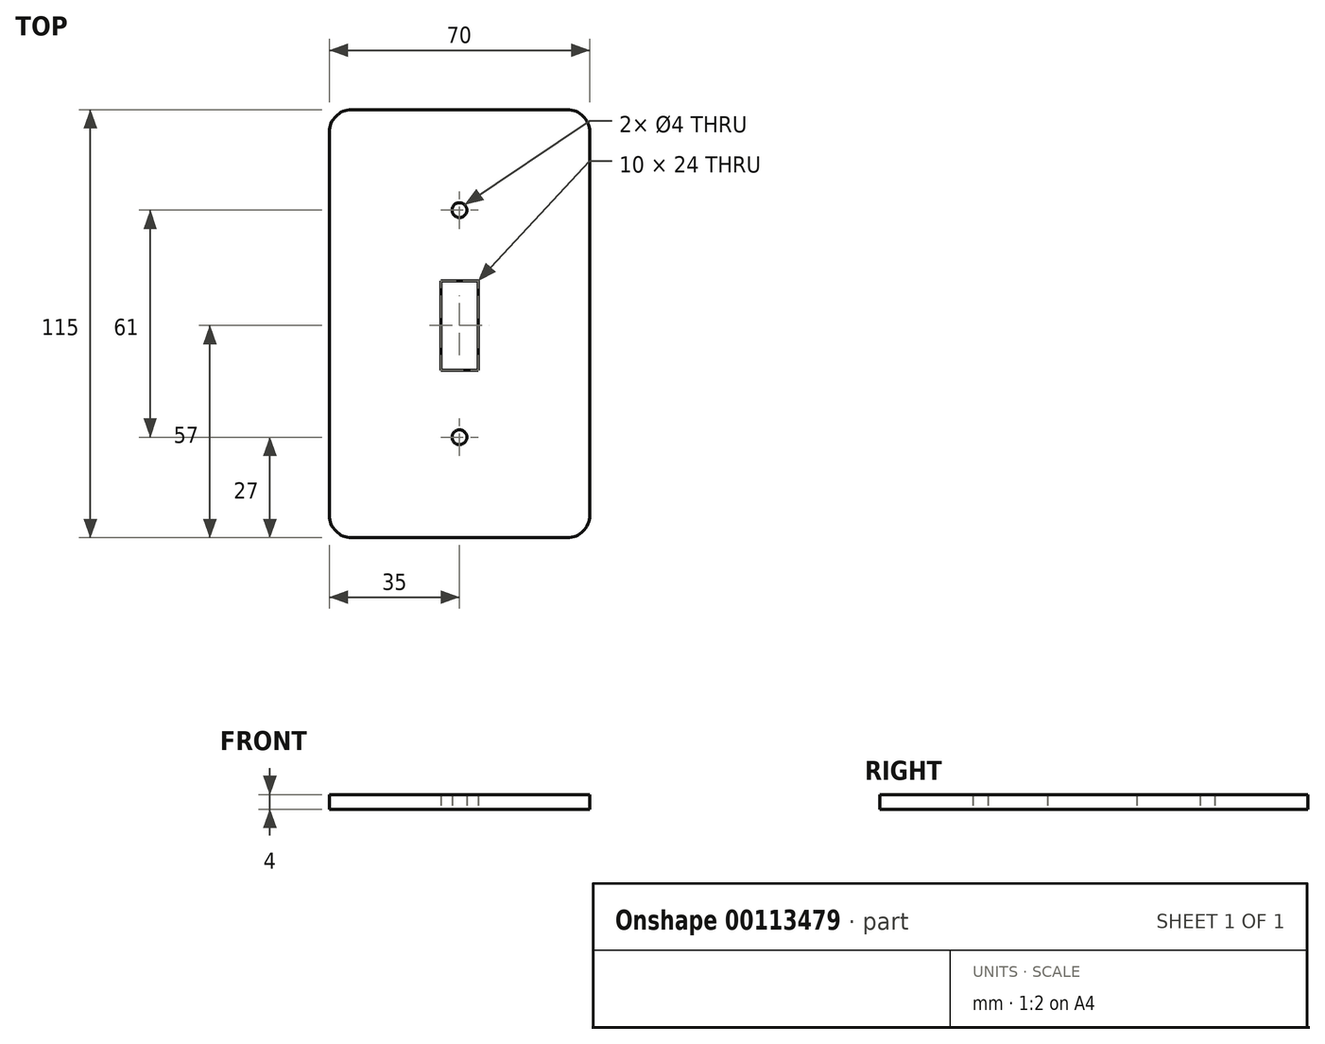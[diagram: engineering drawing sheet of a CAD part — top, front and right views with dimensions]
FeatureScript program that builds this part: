
annotation { "Feature Type Name" : "Feature", "Feature Type Description" : "" }
export const myFeature = defineFeature(function(context is Context, id is Id, definition is map)
    precondition{}
    {
        {
            var Q0;
            Q0=qCreatedBy(makeId("Top.planeOp"),FACE);
            var sketch = newSketch(context, id + "F0", { "sketchPlane" : qUnion([Q0])});
            skLineSegment(sketch, "E0.bottom", {"start": v(0, 0) * mm, "end": v(70, 0) * mm});
            skLineSegment(sketch, "E0.top", {"start": v(0, 115) * mm, "end": v(70, 115) * mm});
            skLineSegment(sketch, "E0.left", {"start": v(0, 0) * mm, "end": v(0, 115) * mm});
            skLineSegment(sketch, "E0.right", {"start": v(70, 0) * mm, "end": v(70, 115) * mm});
            skLineSegment(sketch, "E1.bottom", {"start": v(30, 69) * mm, "end": v(40, 69) * mm});
            skLineSegment(sketch, "E1.top", {"start": v(30, 45) * mm, "end": v(40, 45) * mm});
            skLineSegment(sketch, "E1.left", {"start": v(30, 69) * mm, "end": v(30, 45) * mm});
            skLineSegment(sketch, "E1.right", {"start": v(40, 69) * mm, "end": v(40, 45) * mm});
            skCircle(sketch, "E2", {"center": v(35, 88) * mm, "radius": 2 * mm});
            skCircle(sketch, "E3", {"center": v(35, 27) * mm, "radius": 2 * mm});
            skSolve(sketch);
        }
        {
            var Q0;
            Q0 = qSketchRegion(id + "F0", true);
            extrude(context, id + "F1", {"entities" : qUnion([Q0]), "depth" : 4 * mm});
        }
        {
            var Q0;
            Q0=makeQuery(id+"F1.opExtrude","SWEPT_EDGE",EDGE,{"disambiguationData":[OSD([sQuery(id+"F0.wireOp",EDGE,"E0.top"),sQuery(id+"F0.wireOp",EDGE,"E0.left")])]});
            var Q1;
            Q1=makeQuery(id+"F1.opExtrude","SWEPT_EDGE",EDGE,{"disambiguationData":[OSD([sQuery(id+"F0.wireOp",EDGE,"E0.top"),sQuery(id+"F0.wireOp",EDGE,"E0.right")])]});
            var Q2;
            Q2=makeQuery(id+"F1.opExtrude","SWEPT_EDGE",EDGE,{"disambiguationData":[OSD([sQuery(id+"F0.wireOp",EDGE,"E0.bottom"),sQuery(id+"F0.wireOp",EDGE,"E0.right")])]});
            var Q3;
            Q3=makeQuery(id+"F1.opExtrude","SWEPT_EDGE",EDGE,{"disambiguationData":[OSD([sQuery(id+"F0.wireOp",EDGE,"E0.bottom"),sQuery(id+"F0.wireOp",EDGE,"E0.left")])]});
            fillet(context, id + "F2", {"entities" : qUnion([Q0, Q1, Q2, Q3]), "radius" : 6 * mm, "tangentPropagation" : true, "allowEdgeOverflow" : false});
        }
    });
